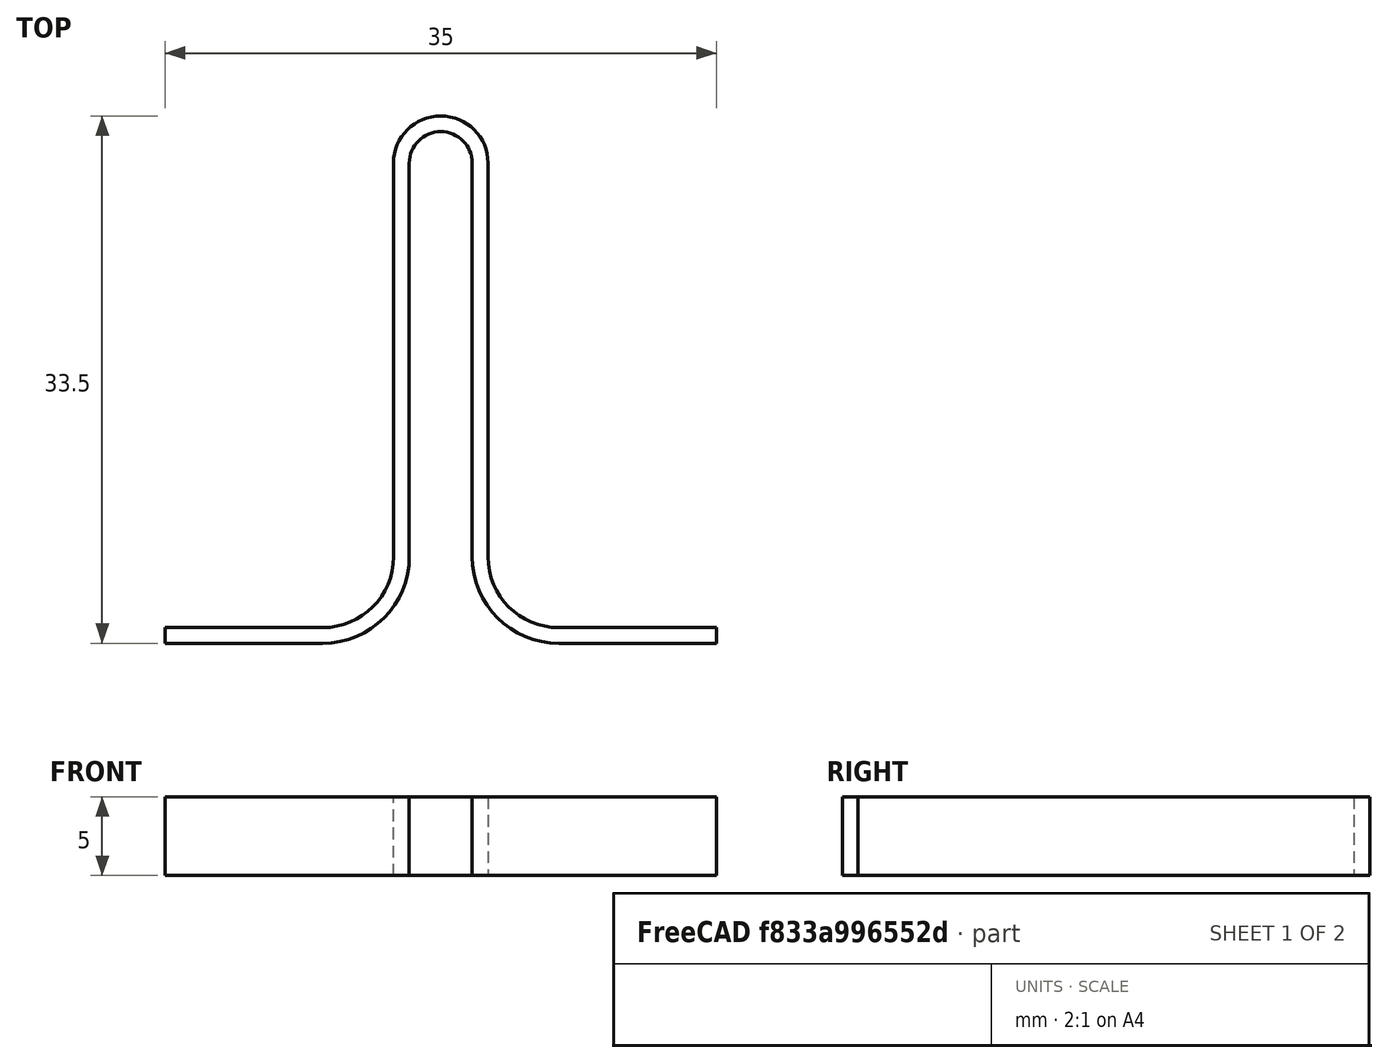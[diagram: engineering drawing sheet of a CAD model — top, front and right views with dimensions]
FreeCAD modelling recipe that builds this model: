
FCSTD DOCUMENT  (FreeCAD 2021.1015R24301 +3962 (Git))
Label: plastic_spring_long_double_loop
License: All rights reserved
objects: Sketcher::SketchObject×2, Spreadsheet::Sheet×1, PartDesign::AdditivePipe×1, PartDesign::Body×1
note: 6 computed .brp shape members not serialized (recipe doc carries the construction recipe); baked Part::Feature solids carry a one-line shape summary decoded from their .brp

FEATURE [Spreadsheet::Sheet] Spreadsheet
  PythonMode = false
  cells = A1='height; B1(h)=5; A2='thickness; B2(thk)=1; A3='dia; B3(dia)=5; A4=start finish rad; B4(r_start)=5; A5=center length; B5(l_center)=30; A6=center spacing; B6(cs)=7; C6=should be dia/2 really; A7=end length; B7(l_end)=10
FEATURE [Sketcher::SketchObject] Sketch  label="profile"
  FullyConstrained = true
  MapMode = 5
  Placement = pos=(0,0,0) rot=(0.57735,0.57735,0.57735;2.0944rad)
  Support = -> [YZ_Plane]
  expr: Constraints[10] = Spreadsheet.thk / 2
  expr: Constraints[11] = Spreadsheet.thk
  expr: Constraints[9] = Spreadsheet.h
  sketch-geometry (4):
    g0: LineSegment StartX=-0.5 StartY=0 StartZ=0 EndX=0.5 EndY=0 EndZ=0
    g1: LineSegment StartX=0.5 StartY=0 StartZ=0 EndX=0.5 EndY=5 EndZ=0
    g2: LineSegment StartX=0.5 StartY=5 StartZ=0 EndX=-0.5 EndY=5 EndZ=0
    g3: LineSegment StartX=-0.5 StartY=5 StartZ=0 EndX=-0.5 EndY=0 EndZ=0
  constraints (12):
    c: Coincident(g0,g1)
    c: Coincident(g1,g2)
    c: Coincident(g2,g3)
    c: Coincident(g3,g0)
    c: Horizontal(g0)
    c: Horizontal(g2)
    c: Vertical(g1)
    c: Vertical(g3)
    c: PointOnObject(g0,g-1)
    c: DistanceY(g3,g3) = 5
    c: DistanceX(g0,g-1) = 0.5
    c: DistanceX(g0,g0) = 1
FEATURE [Sketcher::SketchObject] Sketch001  label="path"
  FullyConstrained = true
  MapMode = 5
  Support = -> [XY_Plane]
  expr: Constraints[12] = Spreadsheet.l_end
  expr: Constraints[13] = Spreadsheet.dia
  expr: Constraints[14] = Spreadsheet.l_end
  expr: Constraints[17] = Spreadsheet.r_start
  expr: Constraints[18] = Spreadsheet.r_start
  expr: Constraints[19] = Spreadsheet.l_center
  expr: Constraints[22] = Spreadsheet.dia
  sketch-geometry (7):
    g0: LineSegment StartX=0 StartY=0 StartZ=0 EndX=10 EndY=0 EndZ=0
    g1: LineSegment StartX=15 StartY=4.99998 StartZ=0 EndX=15 EndY=30 EndZ=0
    g2: ArcOfCircle CenterX=10 CenterY=5 CenterZ=0 NormalX=0 NormalY=0 NormalZ=1 AngleXU=0 Radius=5 StartAngle=4.71239 EndAngle=6.28318
    g3: ArcOfCircle CenterX=17.5 CenterY=30 CenterZ=0 NormalX=0 NormalY=0 NormalZ=1 AngleXU=0 Radius=2.5 StartAngle=6.28318 EndAngle=9.42477
    g4: LineSegment StartX=20 StartY=30 StartZ=0 EndX=20 EndY=5 EndZ=0
    g5: LineSegment StartX=25 StartY=0 StartZ=0 EndX=35 EndY=0 EndZ=0
    g6: ArcOfCircle CenterX=25 CenterY=5 CenterZ=0 NormalX=0 NormalY=0 NormalZ=1 AngleXU=0 Radius=5 StartAngle=3.14159 EndAngle=4.71239
  constraints (24):
    c: Coincident(g0,g-1)
    c: PointOnObject(g0,g-1)
    c: Coincident(g2,g0)
    c: Coincident(g2,g1)
    c: Coincident(g3,g1)
    c: Coincident(g4,g3)
    c: PointOnObject(g5,g-1)
    c: PointOnObject(g5,g-1)
    c: Tangent(g0,g2)
    c: Tangent(g2,g1)
    c: Tangent(g1,g3)
    c: Tangent(g3,g4)
    c: DistanceX(g5,g5) = 10
    c: Diameter(g3) = 5
    c: DistanceX(g0,g0) = 10
    c: Coincident(g6,g4)
    c: Coincident(g6,g5)
    c: Radius(g2) = 5
    c: Radius(g6) = 5
    c: DistanceY(g0,g3) = 30
    c: Tangent(g6,g5)
    c: Tangent(g6,g4)
    c: DistanceX(g1,g4) = 5
    c: Vertical(g1)
FEATURE [PartDesign::AdditivePipe] AdditivePipe
  AuxilleryCurvelinear = true
  AuxillerySpineTangent = false
  Binormal = (0,0,0)
  ClaimChildren = false
  Fit = 0
  FitJoin = 0
  InnerFit = 0
  InnerFitJoin = 0
  Mode = 0
  NewSolid = false
  Placement = pos=(0,0,0) rot=(0.57735,0.57735,0.57735;2.0944rad)
  Profile = -> Sketch
  Spine = -> Sketch001
  SpineTangent = false
  Suppress = false
  Transformation = 0
  Transition = 1
  _ProfileBasedVersion = 1
FEATURE [PartDesign::Body] Body
  AutoGroupSolids = false
  ExportMode = 0
  Group = -> [Sketch,Sketch001,AdditivePipe]
  Origin = -> Origin
  Tip = -> AdditivePipe
  _ExportChildren = -> [AdditivePipe]
  _GroupVersion = 1
